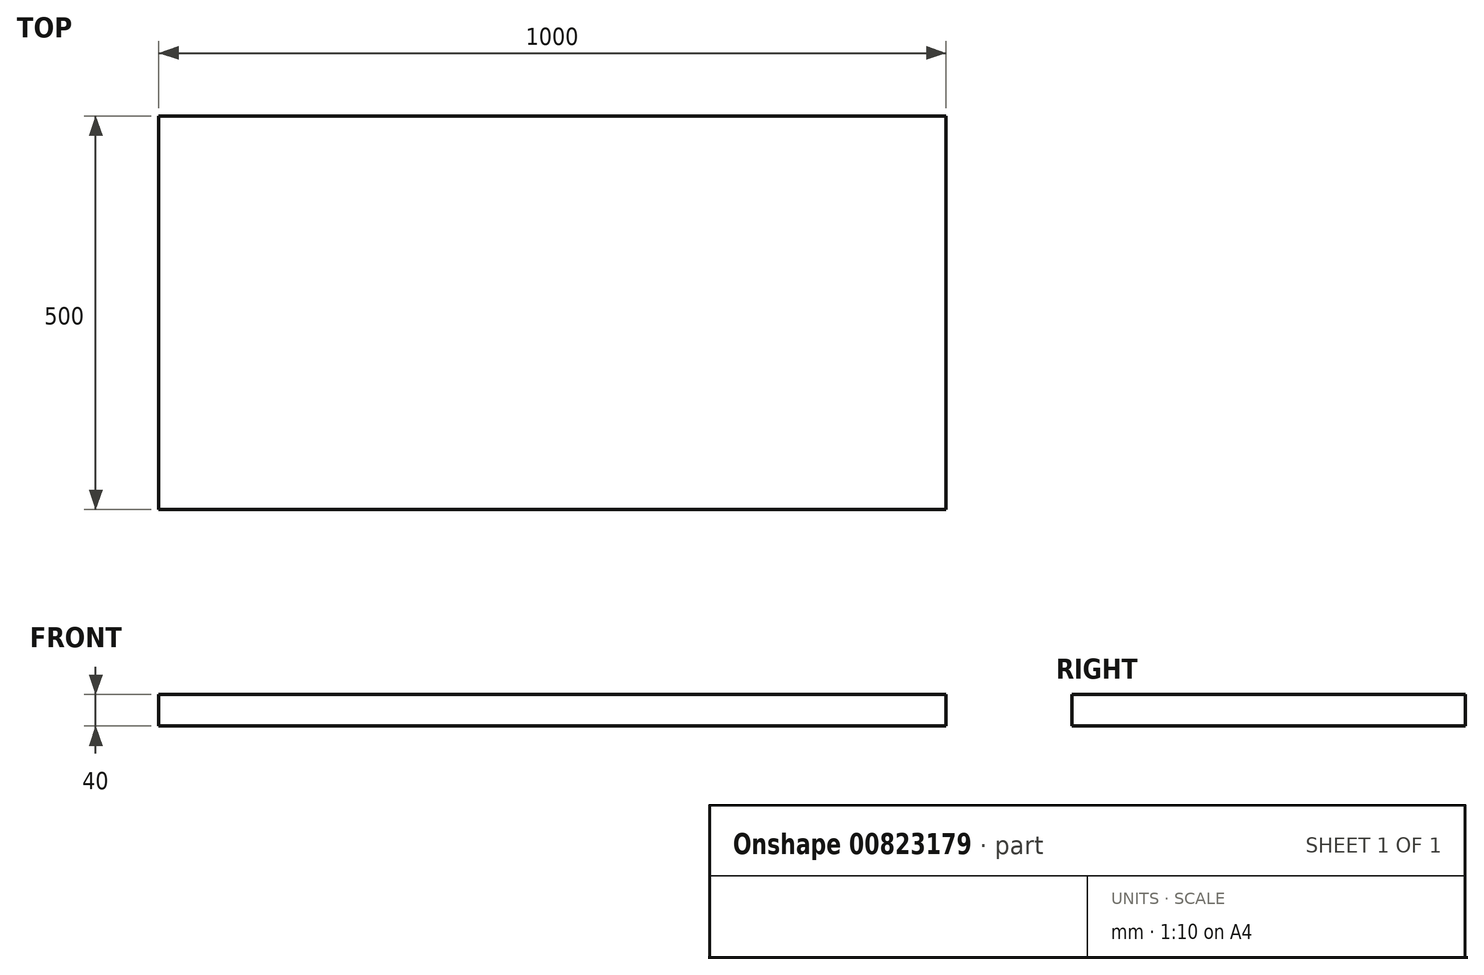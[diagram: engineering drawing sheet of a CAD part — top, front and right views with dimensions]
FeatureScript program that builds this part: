
annotation { "Feature Type Name" : "Feature", "Feature Type Description" : "" }
export const myFeature = defineFeature(function(context is Context, id is Id, definition is map)
    precondition{}
    {
        {
            var Q0;
            Q0=qCreatedBy(makeId("Top.planeOp"),FACE);
            var sketch = newSketch(context, id + "F0", { "sketchPlane" : qUnion([Q0])});
            skLineSegment(sketch, "E0.bottom", {"start": v(-927.16, 424.54) * mm, "end": v(72.84, 424.54) * mm});
            skLineSegment(sketch, "E0.top", {"start": v(-927.16, -75.46) * mm, "end": v(72.84, -75.46) * mm});
            skLineSegment(sketch, "E0.left", {"start": v(-927.16, 424.54) * mm, "end": v(-927.16, -75.46) * mm});
            skLineSegment(sketch, "E0.right", {"start": v(72.84, 424.54) * mm, "end": v(72.84, -75.46) * mm});
            skSolve(sketch);
        }
        {
            var Q0;
            Q0=makeQuery(id+"F0.imprint","IMPRINT",FACE,{"disambiguationData":[TD([[makeQuery(id+"F0.imprint","IMPRINT",EDGE,{"derivedFrom":sQuery(id+"F0.wireOp",EDGE,"E0.bottom")}),-1.0]])]});
            extrude(context, id + "F1", {"entities" : qUnion([Q0]), "depth" : 40 * mm, "offsetDistance" : 25 * mm});
        }
    });
